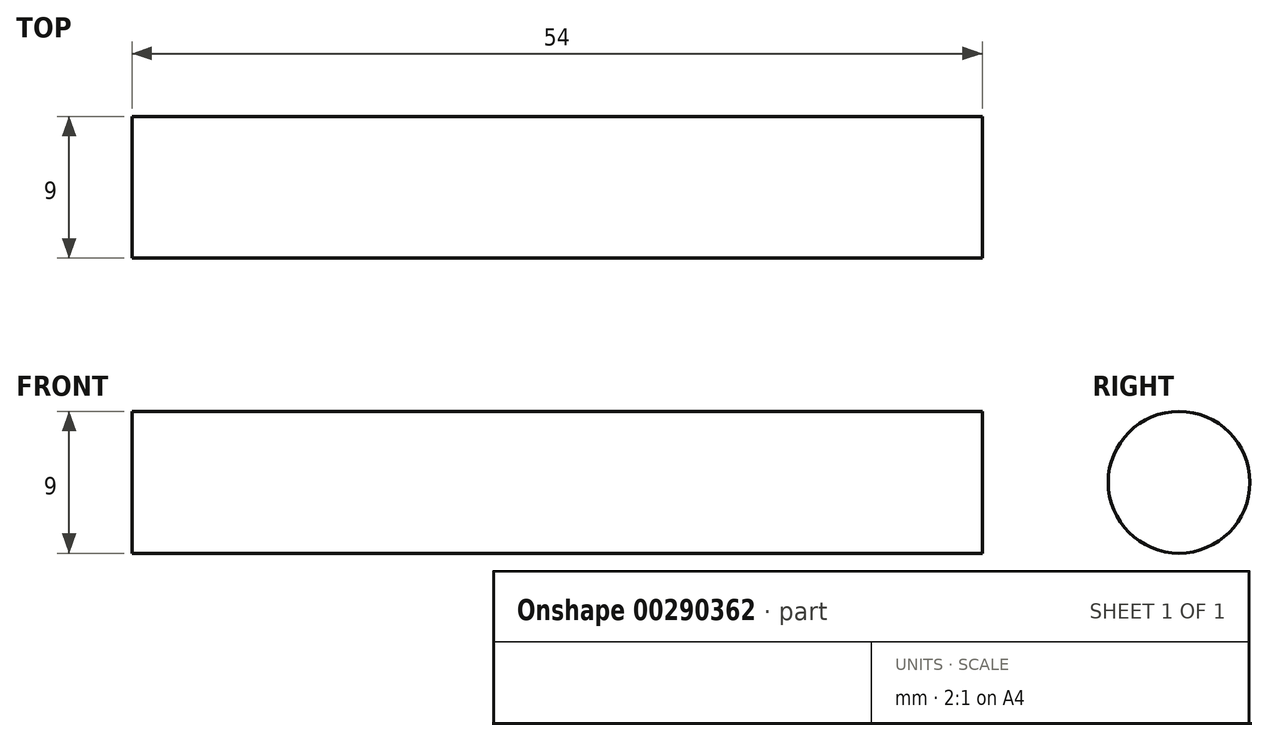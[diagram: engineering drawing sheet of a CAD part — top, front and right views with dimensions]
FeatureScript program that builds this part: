
annotation { "Feature Type Name" : "Feature", "Feature Type Description" : "" }
export const myFeature = defineFeature(function(context is Context, id is Id, definition is map)
    precondition{}
    {
        {
            var Q0;
            Q0=qCreatedBy(makeId("Front.planeOp"),FACE);
            var sketch = newSketch(context, id + "F0", { "sketchPlane" : qUnion([Q0])});
            skLineSegment(sketch, "E0", {"start": v(0, 4.5) * mm, "end": v(27, 4.5) * mm});
            skLineSegment(sketch, "E1", {"start": v(27, 4.5) * mm, "end": v(27, 0) * mm});
            skLineSegment(sketch, "E2.MirrorCS", {"start": v(0, 4.5) * mm, "end": v(-27, 4.5) * mm});
            skLineSegment(sketch, "E3.MirrorCS", {"start": v(-27, 4.5) * mm, "end": v(-27, 0) * mm});
            skLineSegment(sketch, "E4", {"start": v(-27, 0) * mm, "end": v(27, 0) * mm});
            skSolve(sketch);
        }
        {
            var Q0;
            Q0 = qSketchRegion(id + "F0", true);
            var Q1;
            Q1=sQuery(id+"F0.wireOp",EDGE,"E4");
            revolve(context, id + "F1", {"entities" : qUnion([Q0]), "axis" : qUnion([Q1]), "revolveType" : RevolveType.FULL});
        }
    });
